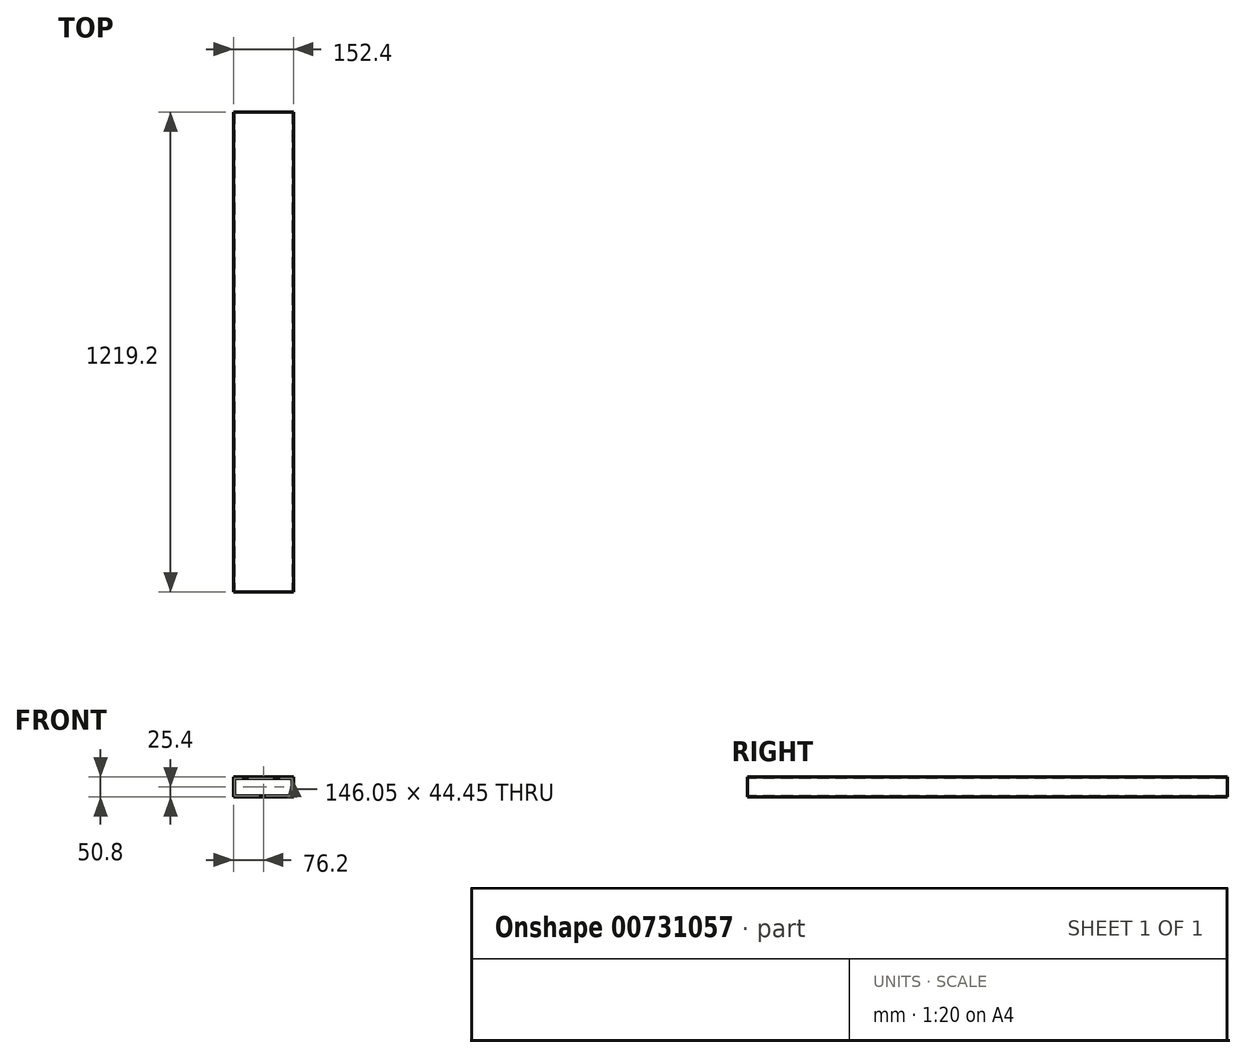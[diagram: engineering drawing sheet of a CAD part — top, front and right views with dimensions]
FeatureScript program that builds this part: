
annotation { "Feature Type Name" : "Feature", "Feature Type Description" : "" }
export const myFeature = defineFeature(function(context is Context, id is Id, definition is map)
    precondition{}
    {
        {
            var Q0;
            Q0=qCreatedBy(makeId("Front.planeOp"),FACE);
            var sketch = newSketch(context, id + "F0", { "sketchPlane" : qUnion([Q0])});
            skLineSegment(sketch, "E0.bottom", {"start": v(0, 0) * mm, "end": v(152.4, 0) * mm});
            skLineSegment(sketch, "E0.top", {"start": v(0, -50.8) * mm, "end": v(152.4, -50.8) * mm});
            skLineSegment(sketch, "E0.left", {"start": v(0, 0) * mm, "end": v(0, -50.8) * mm});
            skLineSegment(sketch, "E0.right", {"start": v(152.4, 0) * mm, "end": v(152.4, -50.8) * mm});
            skLineSegment(sketch, "E1.bottom", {"start": v(3.18, -3.18) * mm, "end": v(149.22, -3.18) * mm});
            skLineSegment(sketch, "E1.top", {"start": v(3.18, -47.62) * mm, "end": v(149.22, -47.62) * mm});
            skLineSegment(sketch, "E1.left", {"start": v(3.18, -3.18) * mm, "end": v(3.18, -47.62) * mm});
            skLineSegment(sketch, "E1.right", {"start": v(149.22, -3.18) * mm, "end": v(149.22, -47.62) * mm});
            skSolve(sketch);
        }
        {
            var Q0;
            Q0=makeQuery(id+"F0.imprint","IMPRINT",FACE,{"disambiguationData":[TD([[makeQuery(id+"F0.imprint","IMPRINT",EDGE,{"derivedFrom":sQuery(id+"F0.wireOp",EDGE,"E0.bottom")}),-1.0]])]});
            extrude(context, id + "F1", {"entities" : qUnion([Q0]), "oppositeDirection" : true, "depth" : 1219.2 * mm, "offsetDistance" : 25.4 * mm});
        }
    });
